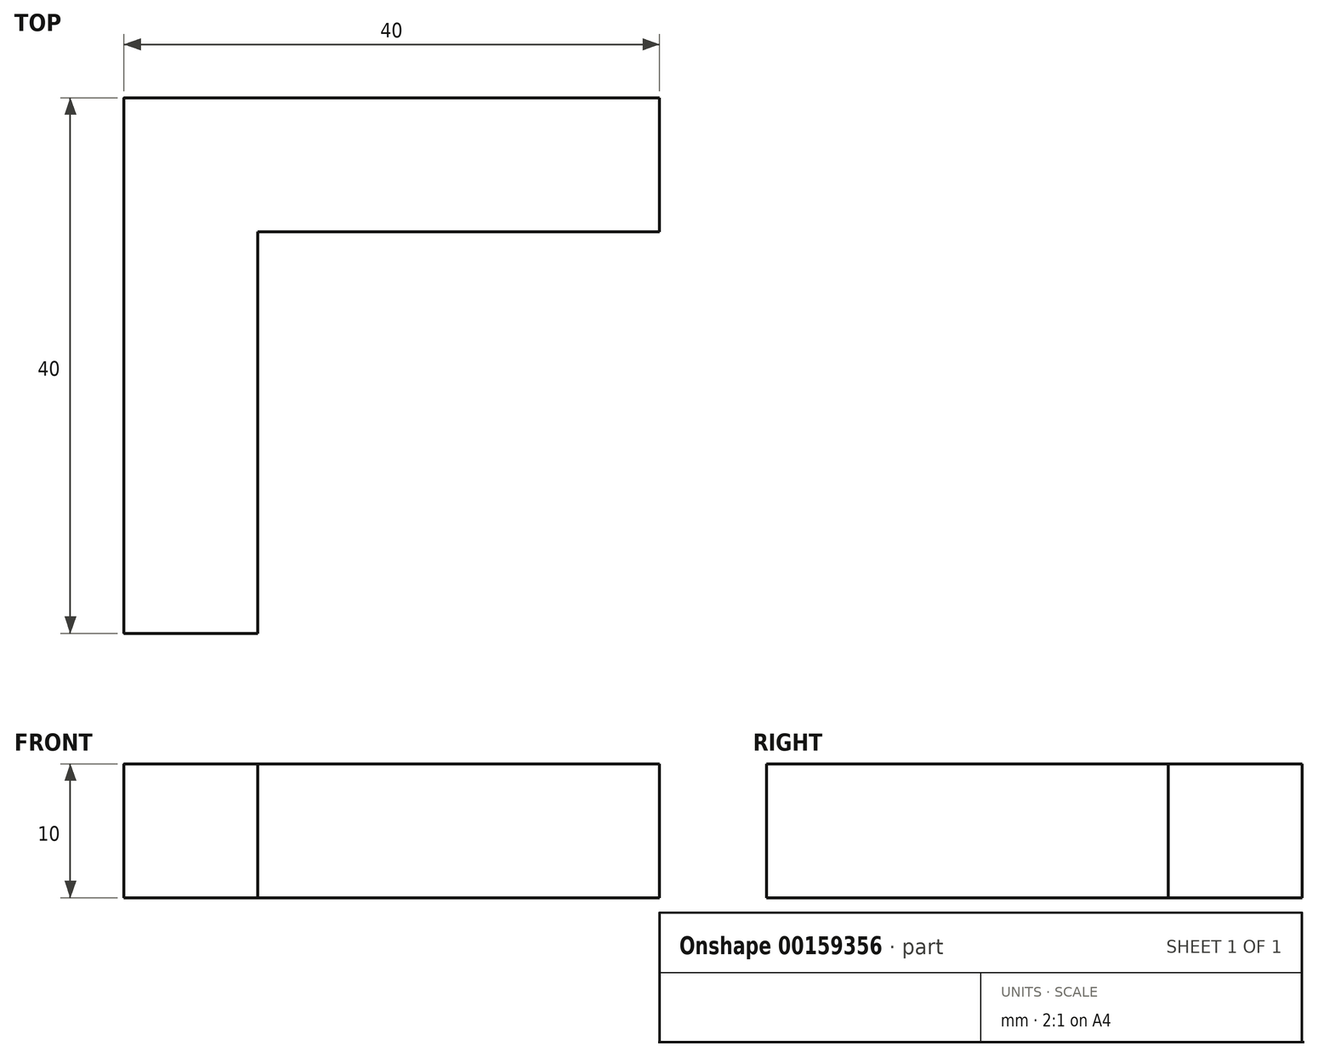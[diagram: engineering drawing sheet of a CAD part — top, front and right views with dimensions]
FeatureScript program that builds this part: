
annotation { "Feature Type Name" : "Feature", "Feature Type Description" : "" }
export const myFeature = defineFeature(function(context is Context, id is Id, definition is map)
    precondition{}
    {
        {
            var Q0;
            Q0=qCreatedBy(makeId("Top.planeOp"),FACE);
            var sketch = newSketch(context, id + "F0", { "sketchPlane" : qUnion([Q0])});
            skLineSegment(sketch, "E0", {"start": v(-35.37, -15.86) * mm, "end": v(-35.37, 24.14) * mm});
            skLineSegment(sketch, "E1", {"start": v(-35.37, 24.14) * mm, "end": v(4.63, 24.14) * mm});
            skLineSegment(sketch, "E2", {"start": v(4.63, 24.14) * mm, "end": v(4.63, 14.14) * mm});
            skLineSegment(sketch, "E3", {"start": v(4.63, 14.14) * mm, "end": v(-25.37, 14.14) * mm});
            skLineSegment(sketch, "E4", {"start": v(-25.37, 14.14) * mm, "end": v(-25.37, -15.86) * mm});
            skLineSegment(sketch, "E5", {"start": v(-25.37, -15.86) * mm, "end": v(-35.37, -15.86) * mm});
            skSolve(sketch);
        }
        {
            var Q0;
            Q0 = qSketchRegion(id + "F0", true);
            extrude(context, id + "F1", {"entities" : qUnion([Q0]), "depth" : 10 * mm});
        }
        {
            var Q0;
            Q0=makeQuery(id+"F1.opExtrude","CAP_EDGE",EDGE,{"disambiguationData":[OSD([sQuery(id+"F0.wireOp",EDGE,"E0")])],"isStart":false});
            fillet(context, id + "F2", {"entities" : qUnion([Q0]), "radius" : 0.02 * mm, "tangentPropagation" : true, "allowEdgeOverflow" : false});
        }
    });
